# Revit family: Sanitary_Showers_hansgrohe_26426CHN-Vernis-Blend-Showerpipe-240-1je_NEW
name_source: partatom
category: Plumbing Fixtures
revit_build: Autodesk Revit 2018 (Build: 20170223_1515(x64)
units: mm (PartAtom-declared; Revit-internal decimal feet)

## family parameters
Cut with Voids When Loaded = Yes
Host = Face
OmniClass Number = 23.31.17.00
OmniClass Title = Showers
Part Type = Normal
Room Calculation Point = No
Round Connector Dimension = Use Diameter
Shared = No

## types (2) — shared parameters
Always visible = Yes
BIMobject category = Showers
Connector Description = Water Inlet 12.7 mm
Default Elevation = 1219 mm
Description = Vernis Blend Showerpipe 240 1jet with thermostat
Design country = Germany
Diameter = 13 mm
Edition number = 1
IFC Classification = Sanitary Terminal
Manufacturer = Hansgrohe
Manufacturer country = Germany
Manufacturer name = hansgrohe
Masterformat 2014 Code = 22 41 23
Masterformat 2014 Description = Residential Showers
Model = 26426CHN
OmniClass Code = 23-31 17 00
OmniClass Description = Showers
Product Guid = 81df033c-5538-4be4-867f-62ce7250a4d8
Product SKU = 26426CHN
Product data url = https://bimobject.com
Product family = Showerpipes with thermostat
Product group = Vernis Blend
Product name = 26426CHN Vernis Blend Showerpipe 240 1jet with thermostat
Product url = https://pro.hansgrohe.com
QR code = https://bimobject.com
UNSPSC Code = 30181503
URL = https://www.hansgrohe.com
Uniclass 2015 Code = Pr_40_20_87_76
Uniclass 2015 Name = Shower heads
Uniformat II Code = D2010
Uniformat II Description = Plumbing Fixtures
Version = 1
Weight Net (Kg) = 3.7

## per-type parameters (varying)
| type | Material |
| 007 Chrome | Hansgrohe - Metal - 007 Chrome |
| 677 Matte Black | Hansgrohe - Metal - 677 Matte Black |

## geometry (parser evidence)
native form markers: Blend x16, Sweep x2
no freeform markers — native parametric forms only
